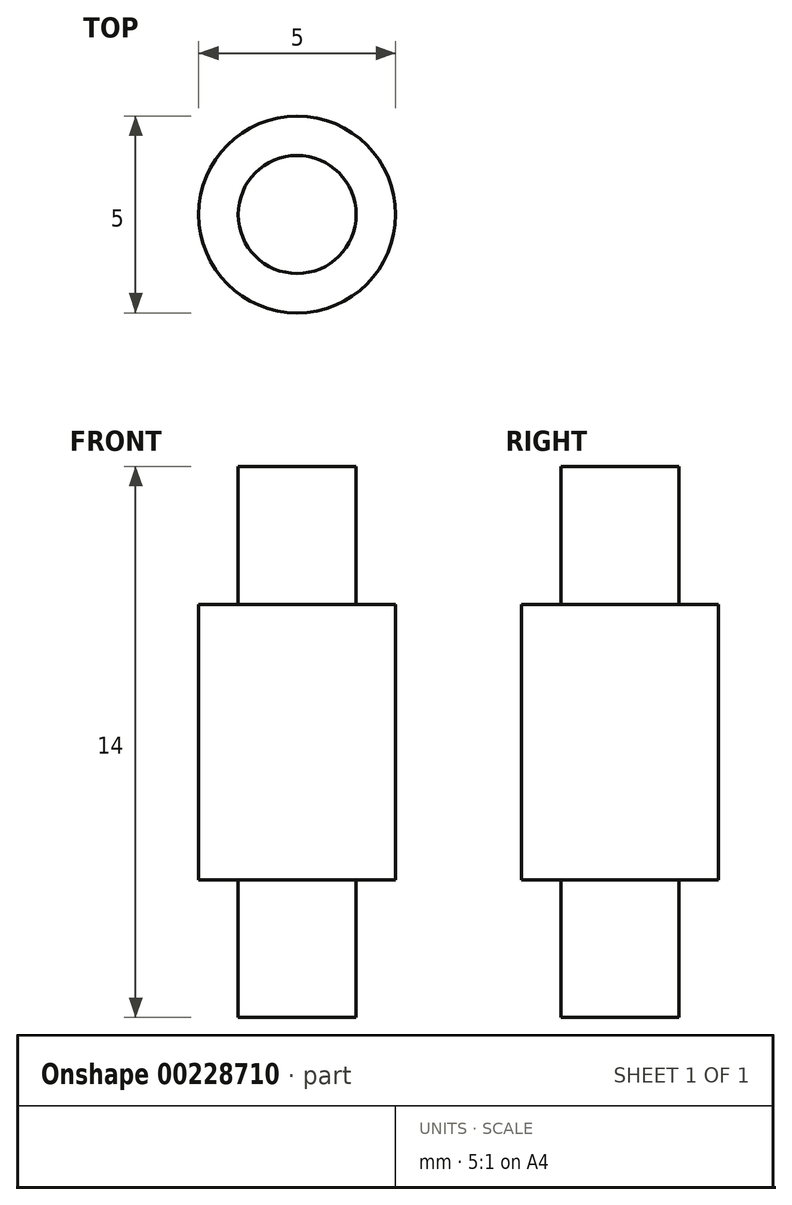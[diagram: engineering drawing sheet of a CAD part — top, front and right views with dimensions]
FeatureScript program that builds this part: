
annotation { "Feature Type Name" : "Feature", "Feature Type Description" : "" }
export const myFeature = defineFeature(function(context is Context, id is Id, definition is map)
    precondition{}
    {
        {
            var Q0;
            Q0=qCreatedBy(makeId("Front.planeOp"),FACE);
            var sketch = newSketch(context, id + "F0", { "sketchPlane" : qUnion([Q0])});
            skLineSegment(sketch, "E0", {"start": v(0, 51.03) * mm, "end": v(-1.5, 51.03) * mm});
            skLineSegment(sketch, "E1", {"start": v(-1.5, 51.03) * mm, "end": v(-1.5, 47.53) * mm});
            skLineSegment(sketch, "E2", {"start": v(-1.5, 47.53) * mm, "end": v(-2.5, 47.53) * mm});
            skLineSegment(sketch, "E3", {"start": v(-2.5, 47.53) * mm, "end": v(-2.5, 44.03) * mm});
            skLineSegment(sketch, "E4.MirrorCS", {"start": v(-2.5, 40.53) * mm, "end": v(-2.5, 44.03) * mm});
            skLineSegment(sketch, "E5.MirrorCS", {"start": v(-1.5, 40.53) * mm, "end": v(-2.5, 40.53) * mm});
            skLineSegment(sketch, "E6.MirrorCS", {"start": v(-1.5, 37.03) * mm, "end": v(-1.5, 40.53) * mm});
            skLineSegment(sketch, "E7.MirrorCS", {"start": v(0, 37.03) * mm, "end": v(-1.5, 37.03) * mm});
            skLineSegment(sketch, "E8", {"start": v(0, 51.03) * mm, "end": v(0, 37.03) * mm});
            skSolve(sketch);
        }
        {
            var Q0;
            Q0=makeQuery(id+"F0.imprint","IMPRINT",FACE,{"disambiguationData":[TD([[makeQuery(id+"F0.imprint","IMPRINT",EDGE,{"derivedFrom":sQuery(id+"F0.wireOp",EDGE,"E0")}),1.0]])]});
            var Q1;
            Q1=sQuery(id+"F0.wireOp",EDGE,"E8");
            revolve(context, id + "F1", {"entities" : qUnion([Q0]), "axis" : qUnion([Q1]), "revolveType" : RevolveType.FULL});
        }
    });
